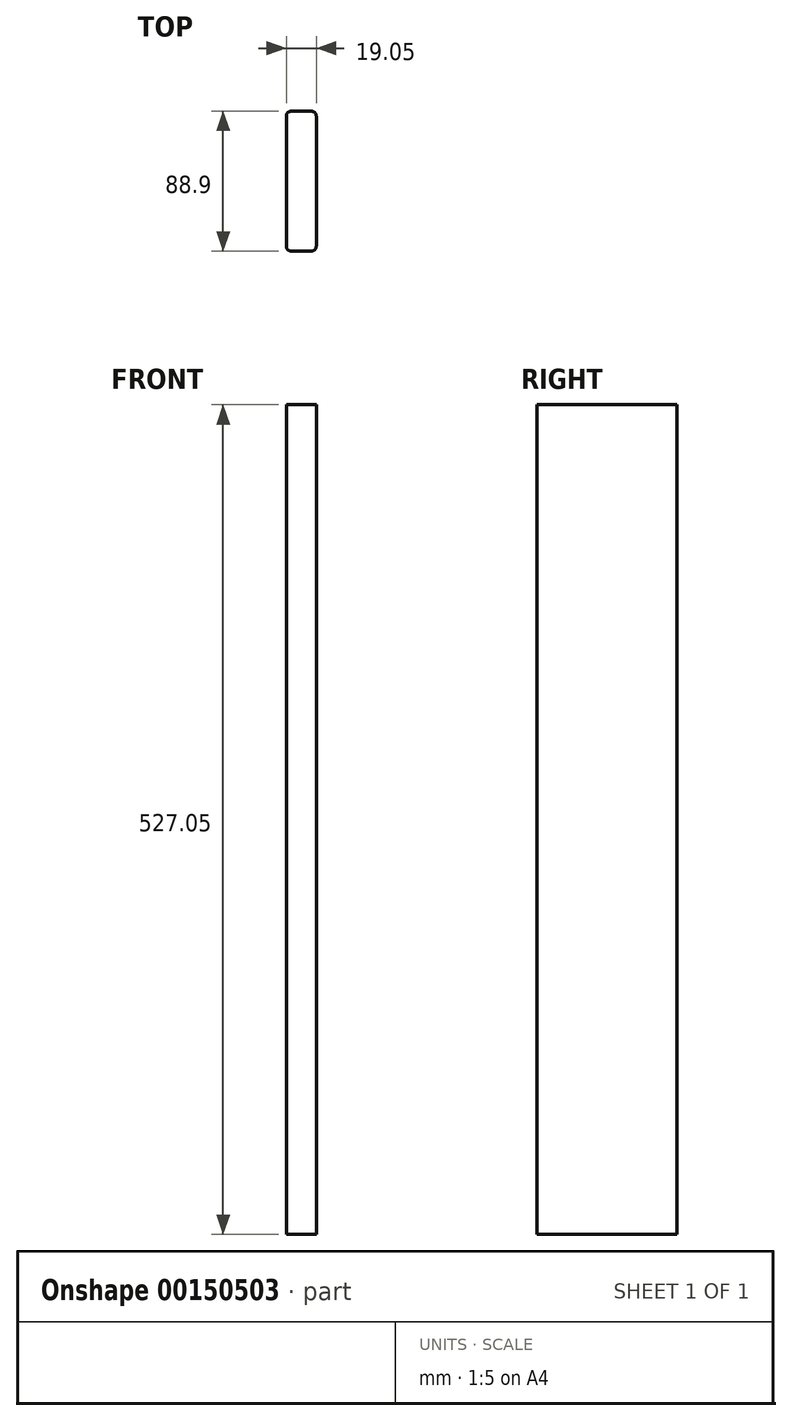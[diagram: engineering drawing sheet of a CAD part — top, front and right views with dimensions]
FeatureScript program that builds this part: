
annotation { "Feature Type Name" : "Feature", "Feature Type Description" : "" }
export const myFeature = defineFeature(function(context is Context, id is Id, definition is map)
    precondition{}
    {
        {
            var Q0;
            Q0=qCreatedBy(makeId("Right.planeOp"),FACE);
            var sketch = newSketch(context, id + "F0", { "sketchPlane" : qUnion([Q0])});
            skLineSegment(sketch, "E0.bottom", {"start": v(-53.15, 258.1) * mm, "end": v(35.75, 258.1) * mm});
            skLineSegment(sketch, "E0.top", {"start": v(-53.15, -268.95) * mm, "end": v(35.75, -268.95) * mm});
            skLineSegment(sketch, "E0.left", {"start": v(-53.15, 258.1) * mm, "end": v(-53.15, -268.95) * mm});
            skLineSegment(sketch, "E0.right", {"start": v(35.75, 258.1) * mm, "end": v(35.75, -268.95) * mm});
            skPoint(sketch, "E1.startSnap0", {"position": v(-8.7, 258.1) * mm});
            skLineSegment(sketch, "E2", {"start": v(-8.7, 124.75) * mm, "end": v(-8.7, 258.1) * mm, "construction": true});
            skLineSegment(sketch, "E3", {"start": v(35.75, 127.3) * mm, "end": v(-53.15, 127.3) * mm, "construction": true});
            skPoint(sketch, "E4", {"position": v(35.75, 127.3) * mm});
            skPoint(sketch, "E5", {"position": v(-53.15, 127.3) * mm});
            skPoint(sketch, "E6", {"position": v(-8.7, 124.75) * mm});
            skSolve(sketch);
        }
        {
            var Q0;
            Q0=makeQuery(id+"F0.imprint","IMPRINT",FACE,{"disambiguationData":[TD([[makeQuery(id+"F0.imprint","IMPRINT",EDGE,{"derivedFrom":sQuery(id+"F0.wireOp",EDGE,"E0.bottom")}),-1.0]])]});
            extrude(context, id + "F1", {"entities" : qUnion([Q0]), "depth" : 19.05 * mm});
        }
        {
            var Q0;
            Q0=makeQuery(id+"F1.opExtrude","CAP_EDGE",EDGE,{"disambiguationData":[OSD([sQuery(id+"F0.wireOp",EDGE,"E0.right")])],"isStart":false});
            var Q1;
            Q1=makeQuery(id+"F1.opExtrude","CAP_EDGE",EDGE,{"disambiguationData":[OSD([sQuery(id+"F0.wireOp",EDGE,"E0.right")])],"isStart":true});
            var Q2;
            Q2=makeQuery(id+"F1.opExtrude","CAP_EDGE",EDGE,{"disambiguationData":[OSD([sQuery(id+"F0.wireOp",EDGE,"E0.left")])],"isStart":false});
            var Q3;
            Q3=makeQuery(id+"F1.opExtrude","CAP_EDGE",EDGE,{"disambiguationData":[OSD([sQuery(id+"F0.wireOp",EDGE,"E0.left")])],"isStart":true});
            fillet(context, id + "F2", {"entities" : qUnion([Q0, Q1, Q2, Q3]), "radius" : 3.17 * mm, "tangentPropagation" : true, "allowEdgeOverflow" : false});
        }
    });
